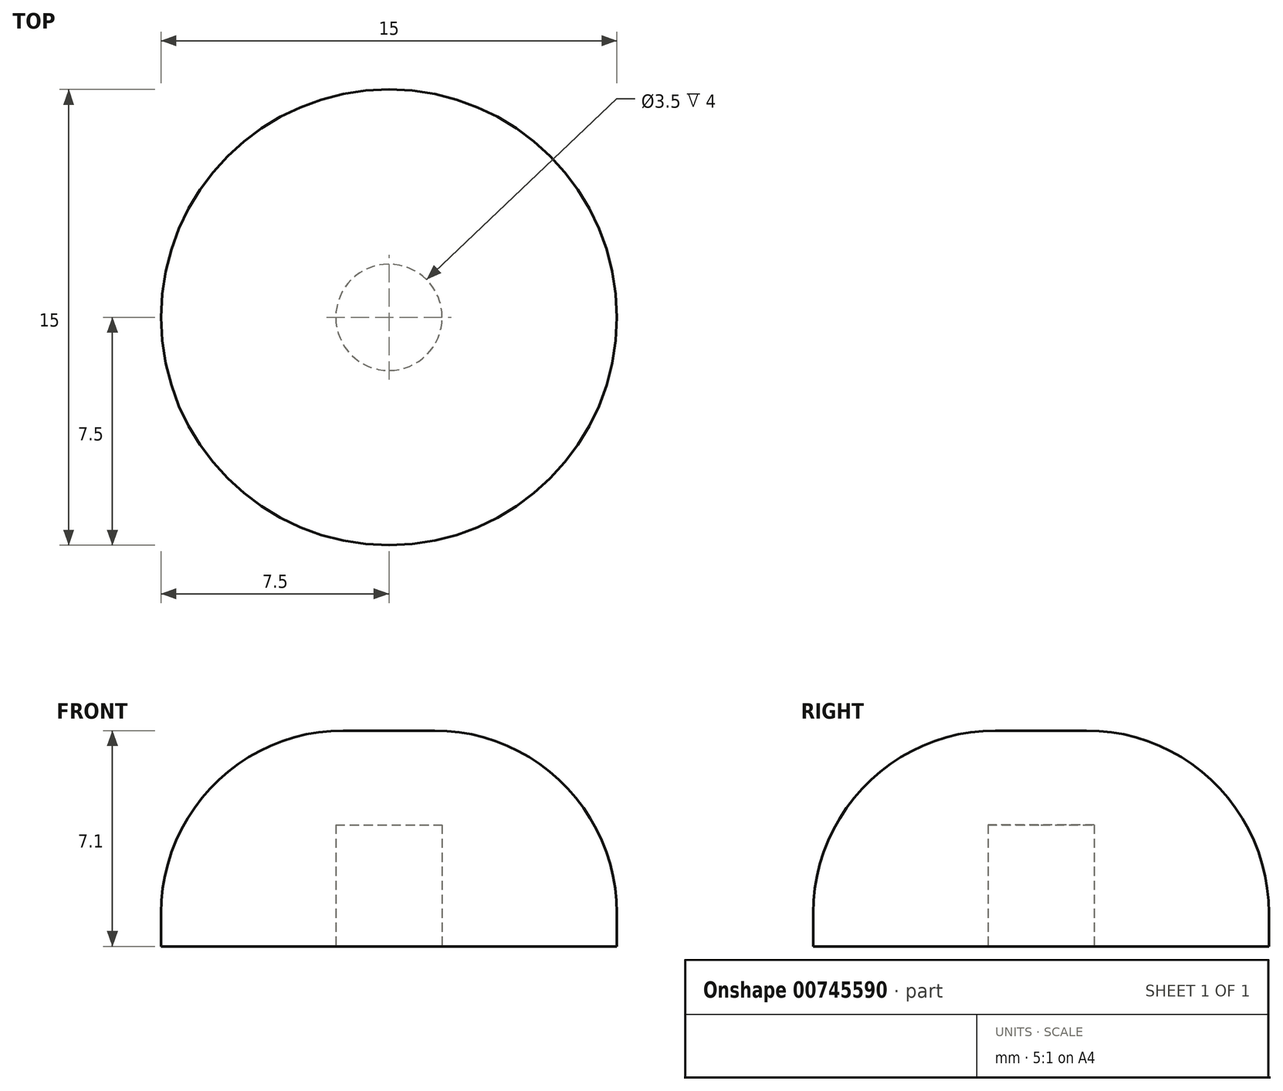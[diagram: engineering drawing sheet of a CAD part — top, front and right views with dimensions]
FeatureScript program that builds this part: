
annotation { "Feature Type Name" : "Feature", "Feature Type Description" : "" }
export const myFeature = defineFeature(function(context is Context, id is Id, definition is map)
    precondition{}
    {
        {
            var Q0;
            Q0=qCreatedBy(makeId("Top.planeOp"),FACE);
            var sketch = newSketch(context, id + "F0", { "sketchPlane" : qUnion([Q0])});
            skCircle(sketch, "E0", {"center": v(0, 0) * mm, "radius": 7.5 * mm});
            skSolve(sketch);
        }
        {
            var Q0;
            Q0=makeQuery(id+"F0.imprint","IMPRINT",FACE,{"disambiguationData":[TD([[makeQuery(id+"F0.imprint","IMPRINT",EDGE,{"derivedFrom":sQuery(id+"F0.wireOp",EDGE,"E0")}),1.0]])]});
            extrude(context, id + "F1", {"entities" : qUnion([Q0]), "depth" : 7.1 * mm, "offsetDistance" : 25 * mm});
        }
        {
            var Q0;
            Q0=makeQuery(id+"F1.opExtrude","CAP_FACE",FACE,{"disambiguationData":[OSD([sQuery(id+"F0.wireOp",EDGE,"E0")])],"isStart":true});
            var sketch = newSketch(context, id + "F2", { "sketchPlane" : qUnion([Q0])});
            skCircle(sketch, "E1", {"center": v(0, 0) * mm, "radius": 1.75 * mm});
            skSolve(sketch);
        }
        {
            var Q0;
            Q0 = qSketchRegion(id + "F2", true);
            extrude(context, id + "F3", {"entities" : qUnion([Q0]), "operationType" : NewBodyOperationType.REMOVE, "oppositeDirection" : true, "depth" : 4 * mm, "offsetDistance" : 25 * mm});
        }
        {
            var Q0;
            Q0=makeQuery(id+"F1.opExtrude","CAP_EDGE",EDGE,{"disambiguationData":[OSD([sQuery(id+"F0.wireOp",EDGE,"E0")])],"isStart":false});
            fillet(context, id + "F4", {"entities" : qUnion([Q0]), "radius" : 6 * mm, "tangentPropagation" : true, "allowEdgeOverflow" : false});
        }
    });
